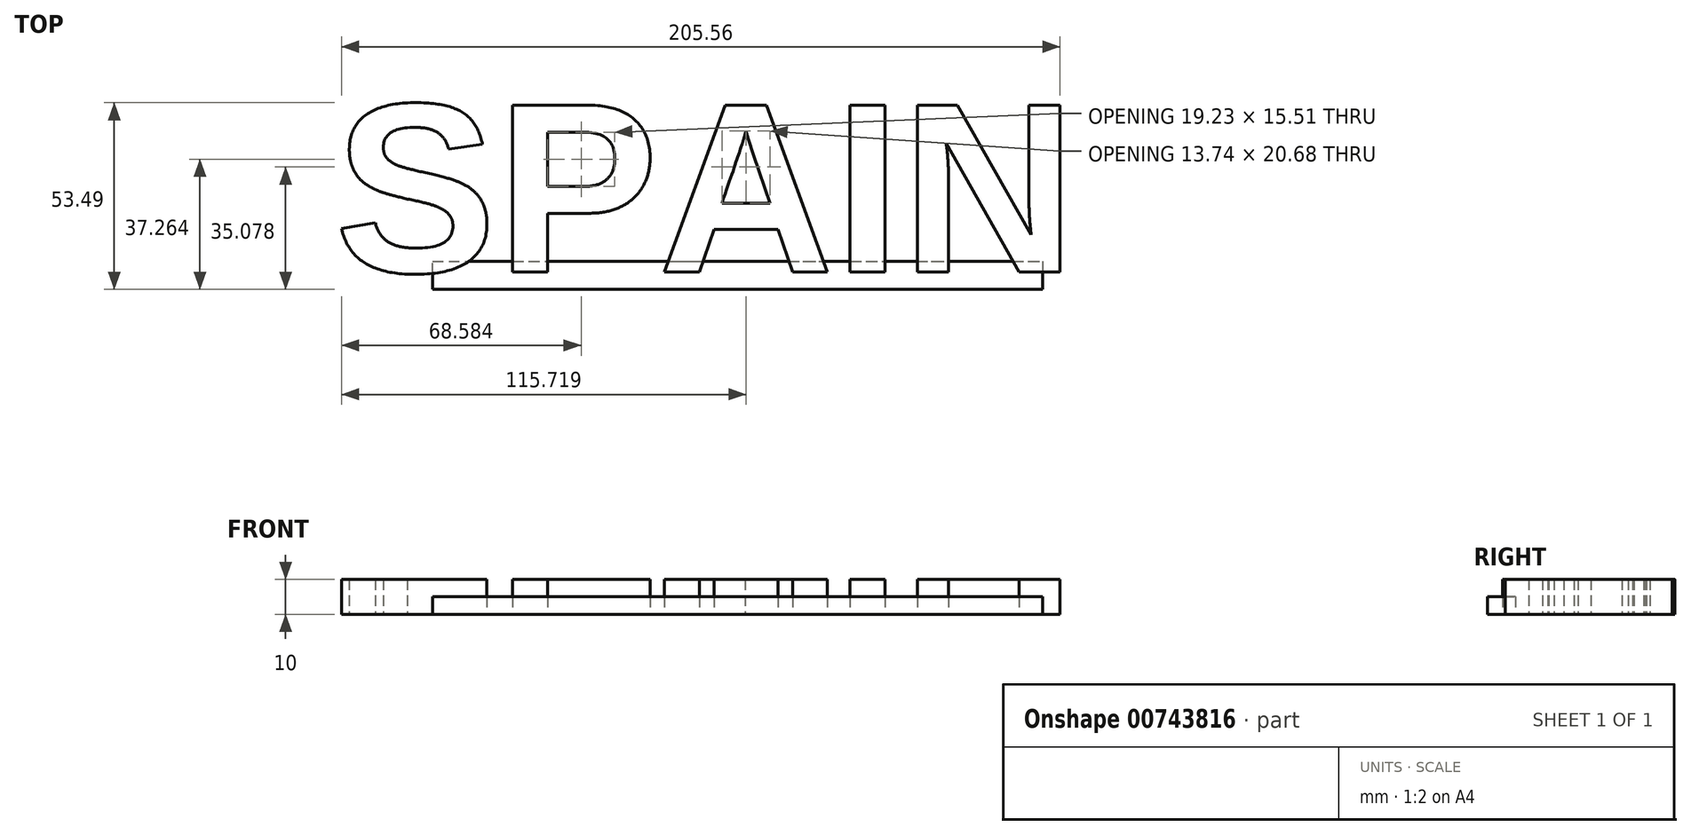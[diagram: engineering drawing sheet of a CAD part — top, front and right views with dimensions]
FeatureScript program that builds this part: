
annotation { "Feature Type Name" : "Feature", "Feature Type Description" : "" }
export const myFeature = defineFeature(function(context is Context, id is Id, definition is map)
    precondition{}
    {
        {
            var Q0;
            Q0=qCreatedBy(makeId("Top.planeOp"),FACE);
            var sketch = newSketch(context, id + "F0", { "sketchPlane" : qUnion([Q0])});
            skText(sketch, "E0", { "text": "SPAIN", "fontName": "Arimo-Bold.ttf"});
            const initialGuessF0  = {"E0": [-0.09335, 0, 1, 0, 0.05]};
            skSetInitialGuess(sketch, initialGuessF0);
            skSolve(sketch);
        }
        {
            var Q0;
            Q0 = qSketchRegion(id + "F0", true);
            extrude(context, id + "F1", {"entities" : qUnion([Q0]), "depth" : 10 * mm, "offsetDistance" : 25 * mm});
        }
        {
            var Q0;
            Q0=qCreatedBy(makeId("Top.planeOp"),FACE);
            var sketch = newSketch(context, id + "F2", { "sketchPlane" : qUnion([Q0])});
            skLineSegment(sketch, "E1", {"start": v(-65.23, 3) * mm, "end": v(109.21, 3) * mm});
            skLineSegment(sketch, "E2", {"start": v(109.21, 3) * mm, "end": v(109.21, -5) * mm});
            skLineSegment(sketch, "E3", {"start": v(109.21, -5) * mm, "end": v(-65.23, -5) * mm});
            skLineSegment(sketch, "E4", {"start": v(-65.23, -5) * mm, "end": v(-65.23, 3) * mm});
            skSolve(sketch);
        }
        {
            var Q0;
            Q0 = qSketchRegion(id + "F2", true);
            extrude(context, id + "F3", {"entities" : qUnion([Q0]), "depth" : 5 * mm, "offsetDistance" : 25 * mm});
        }
    });
